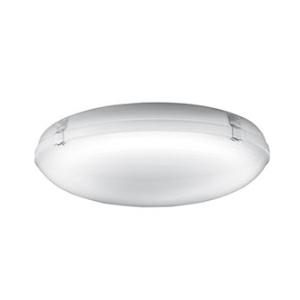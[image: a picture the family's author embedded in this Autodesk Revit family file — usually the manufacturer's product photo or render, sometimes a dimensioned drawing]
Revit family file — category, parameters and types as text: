
# Revit family: 3f_filippi_-_3f_petra_sensor_3f_filippi_-_34233_-_3f_petra_op_300_12w_led_sensor
name_source: partatom
category: Lighting Fixtures
units: mm (PartAtom-declared; Revit-internal decimal feet)

## family parameters
Cut with Voids When Loaded = No
Host = Face
Light Source = No
Part Type = Normal
Room Calculation Point = No
Round Connector Dimension = Use Diameter
Shared = No

## types (1)
- 3F Filippi - 3F Petra Sensor (1 x LED, 1660 lm, 15 W, 4000 K)
    Apparent Load = 15 VA
    Approval mark = ENEC
    CIE Flux Codes = 42 72 90 90 100
    Color Rendering = 80
    Color Temperature = 4000 K
    Control Gear = Electronic ballast
    Default Elevation = 1800 mm
    Description = ILLUMINOTECHNICAL
Luminous efficiency 100% (DLOR 90%, ULOR 10%).
Initial luminous flux of the luminaire 1660 lm.
Diffused symmetric distribution.
Installation Interdistance Transv.D = 1.26 x hu - Long.D = 1.26 x hu.
Tabular UGR (CIE 117 - 4H-8H; S=0.25H; 70/50/20): RUG 20.8 - 20.8.
Beam angle: 118° - 117°.
Luminous efficacy 111 lm/W.
Lifetime (L93/B10): 30000 h. (tq+25°C)
Lifetime (L90/B10): 50000 h. (tq+25°C)
Lifetime (L85/B10): 80000 h. (tq+25°C)
Lifetime (L80/B10): 100000 h. (tq+25°C)
Sudden decreased luminous flux after 50000 hours: 0% (C0).
Photobiological safety in compliance with IEC/TR 62778: RG0 risk exempt, (IEC 62471).
In compliance with IEC/EN 62722-2-1 - IEC/EN 62717 standards.

SOURCE
Circular LED module 12W/840.
Energy efficiency class (UE 2019/2020 - UE 2019/2015): D.
CIE 13.3 Colour rendering index: CRI >80 (R9 <50%).
IES TM-30 Fidelity Index: Rf = 84 Rg = 95.
CCT nominal colour temperature 4000 K.
Colour initial tolerance (MacAdam): SDCM 3.

MECHANICAL
Housing in glazed self-extinguishing V2 polycarbonate, UV stabilised, injection moulded.
Ecologic anti-aging injected sealing gasket.
Gear-tray reflector unit in aluminium, painted in white polyester, fixed to the housing by quick-fastening steel devices, hinged opening.
Diffuser in opal methacrylate (PMMA), injection moulded.
Snug fit safety snap-lock clips for diffuser mounting in transparent polycarbonate, screwdriver opening.
Luminaire with limited surface temperature. - D - (EN 60598-2-24)
Dimensions: diameter 300 mm, height 120 mm. Weight 0.985 kg.
IP64 protection degree.
Mechanical strength to impacts IK02 (0.2 joule).
Glow-wire test resistance 650°C.

ELECTRICAL
Halogen Free electronic wiring 230V-50/60Hz, power factor 0.60, THD <25%, constant output current, SELV, class I, 1 driver.
High frequency radar motion sensor, integrated in the luminarie.
Power of the luminaire 15 W.
CE - IEC 60598-1 - EN 60598-1.
SAFE FLICKER: PstLM=<1 and SVM=<0.4 (IEC TR 61547-1 and IEC TR 63158), to ensure a more comfortable and safe light.
Ambient temperature from 0°C to +25°C.
Temperature class T6 max 85°C.
Relative humidity UR: <85%.

INSTALLATION
Ceiling / Wall.

APPLICATIONS
Suitable product for food production plants (HACCP), IFS (Food Version 6), BRC (GSFS Food Version 7).
Transit areas, stairwells. Environments where a diffused lighting provides visual comfort.
Virtually in all environments compatibly with the emissions/atmospheres compromising the use of plastic materials.
Not suitable for installation on surfaces subject to important vibrations, exposed to weather conditions.

LIGHT MANAGEMENT
The radar movement sensor, integrated in the device, allows switching on/off as a result of presence detection and the set twilight threshold.
Recommended installation height on ceiling up to 4 m and on wall up to 2.7 m.

WARNING
Luminaire designed for disposal/recycling at end-of-life.
Replaceable (LED only) light source by a professional. Replaceable control gear by a professional.
    Height = 120 mm
    Lamp = 1 x LED
    Lamp Light Flux = 1660 lm
    Lamp Power = 15 W
    Lamp count = 1
    Length = 300 mm
    Lifetime = 50000 h
    Luminous efficacy = 111 lm/W
    Manufacturer = 3F Filippi
    ModVariant = No
    Model = 3F Filippi - 34233 - 3F Petra OP 300 12W LED Sensor
    Mounting Place = Ceiling
    Mounting Type = Surface mounted
    Number of Poles = 1
    OnlyDefault = Yes
    Power Factor = 1
    Product Name = 3F Filippi - 3F Petra Sensor
    Product group = ceiling mounted luminaire
    ProductGroupID = 3
    Protection Class = Protection class I
    Protection Degree = IP 64
    RLX_Detail_Level = 1
    RLX_Emergency_Light_Flux = 0 lm
    RLX_Emergency_Type = 0
    RLX_Emergency_Type_DB = No
    RlxData = <blob elided: 207413 chars, md5=061733e3>
    Socket = socket
    Standby Power = 0 W
    System Light Flux = 1660 lm
    System Power = 15 W
    Type Comments = Product without accessories
    Type Image = 3ffilippi_34233.jpg
    URL = http://relux.com
    VarID = ---
    Voltage = 0 V
    Weight = 0.00 kg
    Width = 0 mm  [stored 0 ft]

note: [stored X ft] marks values corroborated as IEEE doubles in the binary element streams (Revit-internal decimal feet)

## geometry (parser evidence)
native form markers: Blend x4, Sweep x12
no freeform markers — native parametric forms only
